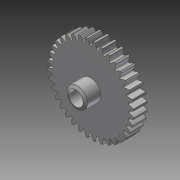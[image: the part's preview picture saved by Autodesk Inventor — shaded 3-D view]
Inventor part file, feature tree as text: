
AUTODESK INVENTOR PART (.ipt)
format: ipt  version: 2014 SP1 (Build 180222100, 222)  size: 468,992 bytes
history: native  units: in
note: dims shown in document units (in); Inventor stores cm internally (conversion verified against a paired STEP export)
features: chamfer x1, other x1, imported_body x1
ambient origin geometry x8: Origin, YZ Plane, XZ Plane, XY Plane, X Axis, Y Axis, Z Axis, Center Point
bodies: Body1 (feature_tree)
feature tree (3):
  chamfer  "Chamfer1"  [1 undecoded]
  other  "217-2428-016 Rev2_Spur01.ipt1"
  imported_body  "Base1"
note: 1 required parameter value undecoded (feature->parameter linkage not recoverable at this tier; creation-order binding heuristic only, values carry confidence <= 0.55)
